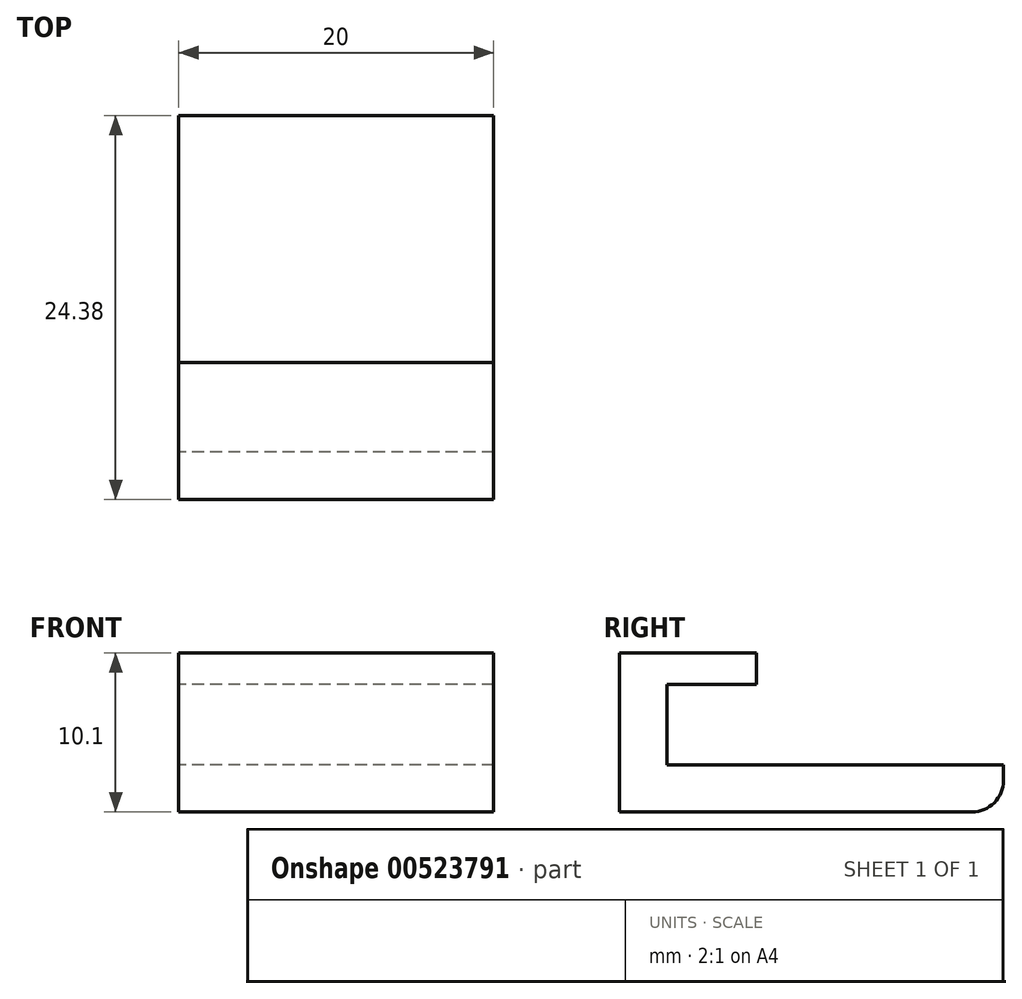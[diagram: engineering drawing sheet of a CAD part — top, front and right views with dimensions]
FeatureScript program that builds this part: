
annotation { "Feature Type Name" : "Feature", "Feature Type Description" : "" }
export const myFeature = defineFeature(function(context is Context, id is Id, definition is map)
    precondition{}
    {
        {
            var Q0;
            Q0=qCreatedBy(makeId("Right.planeOp"),FACE);
            var sketch = newSketch(context, id + "F0", { "sketchPlane" : qUnion([Q0])});
            skLineSegment(sketch, "E0.bottom", {"start": v(-1.58, -5.84) * mm, "end": v(-23.96, -5.84) * mm});
            skLineSegment(sketch, "E0.top", {"start": v(0.42, -2.84) * mm, "end": v(-20.96, -2.84) * mm});
            skLineSegment(sketch, "E1", {"start": v(-23.96, 4.26) * mm, "end": v(-15.26, 4.26) * mm});
            skLineSegment(sketch, "E2", {"start": v(-15.26, 4.26) * mm, "end": v(-15.26, 2.26) * mm});
            skLineSegment(sketch, "E3", {"start": v(-15.26, 2.26) * mm, "end": v(-20.96, 2.26) * mm});
            skLineSegment(sketch, "E4", {"start": v(-20.96, 2.26) * mm, "end": v(-20.96, -2.84) * mm});
            skLineSegment(sketch, "E5", {"start": v(-23.96, 4.26) * mm, "end": v(-23.96, -5.84) * mm});
            skLineSegment(sketch, "E6", {"start": v(0.42, -2.84) * mm, "end": v(0.42, -3.84) * mm});
            skPoint(sketch, "E7.visualSharp", {"position": v(0.42, -5.84) * mm});
            skArc(sketch, "E7.filletArc", {"start": v(-1.58, -5.84) * mm, "mid": v(-0.16, -5.26) * mm, "end": v(0.42, -3.84) * mm});
            skSolve(sketch);
        }
        {
            var Q0;
            Q0=makeQuery(id+"F0.imprint","IMPRINT",FACE,{"disambiguationData":[TD([[makeQuery(id+"F0.imprint","IMPRINT",EDGE,{"derivedFrom":sQuery(id+"F0.wireOp",EDGE,"E0.bottom")}),-1.0]])]});
            extrude(context, id + "F1", {"entities" : qUnion([Q0]), "depth" : 20 * mm, "offsetDistance" : 25 * mm});
        }
    });
